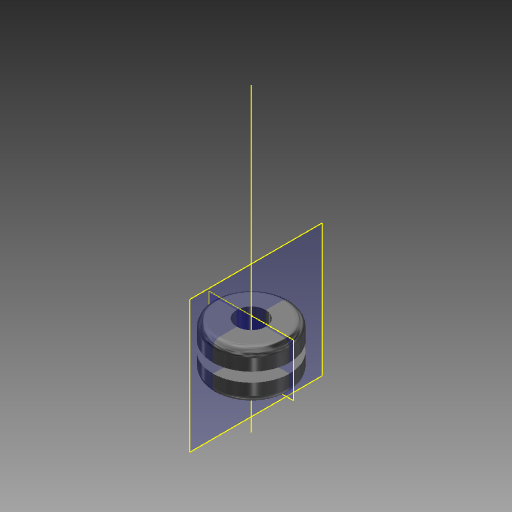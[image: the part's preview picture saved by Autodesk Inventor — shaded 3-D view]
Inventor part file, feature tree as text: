
AUTODESK INVENTOR PART (.ipt)
format: ipt  version: 2017.1 (Build 211199000, 199)  size: 145,920 bytes
history: native  units: in
note: dims shown in document units (in); Inventor stores cm internally (conversion verified against a paired STEP export)
features: plane x2, revolve x1, sketch x1, other x1
ambient origin geometry x8: Origin, YZ Plane, XZ Plane, XY Plane, X Axis, Y Axis, Z Axis, Center Point
bodies: Solid1 (feature_tree)
feature tree (5):
  plane  "Work Plane2"
  revolve  "Revolution1"  Angle=90.0deg
  plane  "Work Plane3"
  sketch  "Sketch2"  dims[d0=0.05in d1=90.0deg d2=0.05in d4=0.1562in d5=0.3125in d6=90.0deg]
  other  "Work Axis2"
